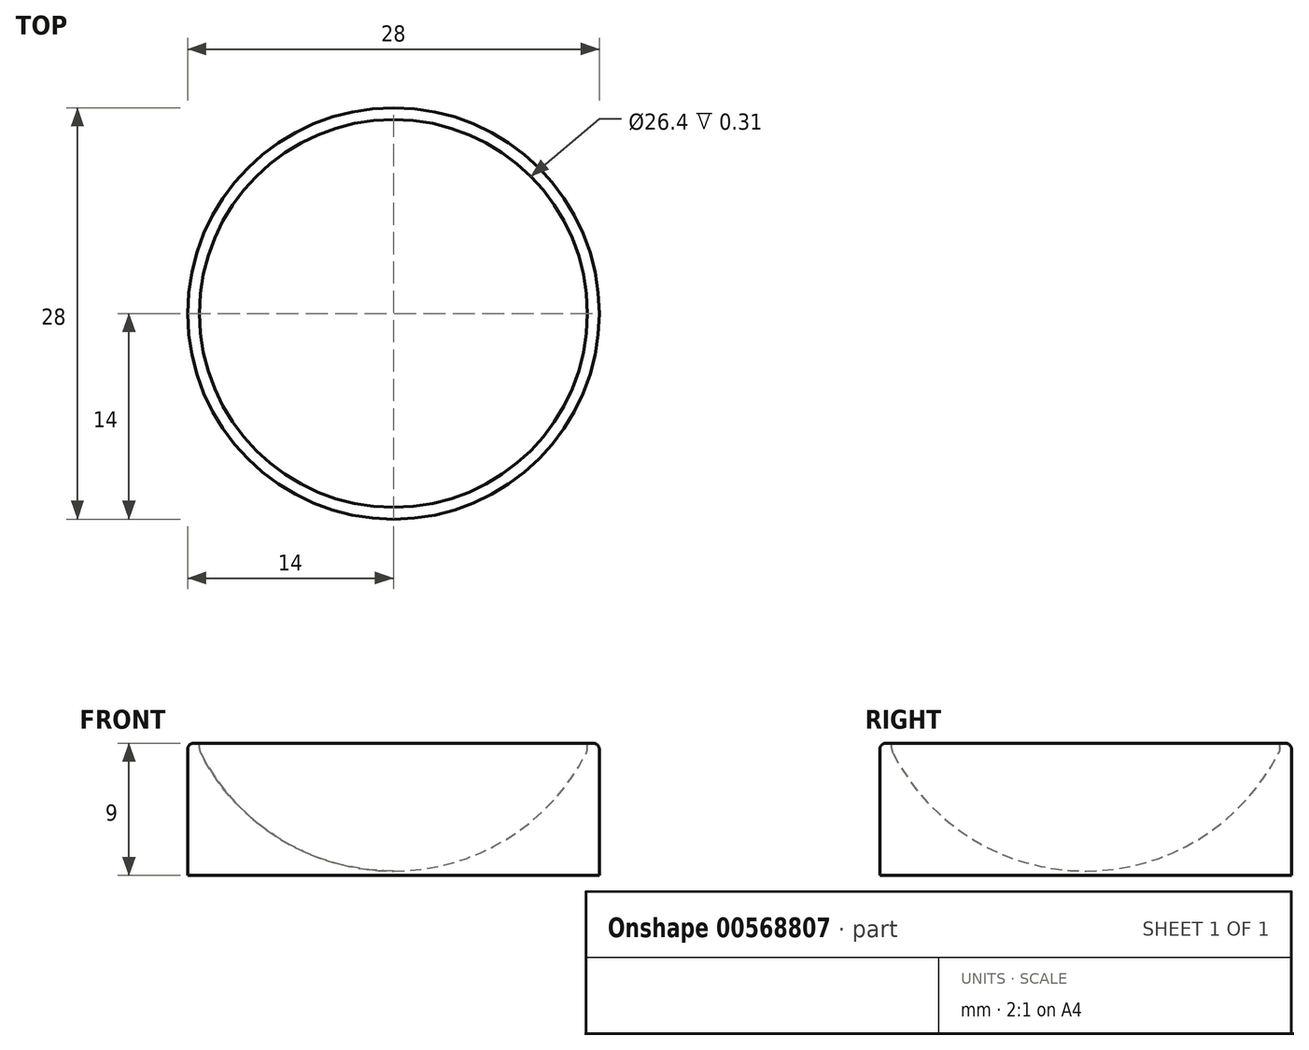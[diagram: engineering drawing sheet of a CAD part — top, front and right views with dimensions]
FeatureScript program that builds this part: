
annotation { "Feature Type Name" : "Feature", "Feature Type Description" : "" }
export const myFeature = defineFeature(function(context is Context, id is Id, definition is map)
    precondition{}
    {
        {
            var Q0;
            Q0=qCreatedBy(makeId("Front.planeOp"),FACE);
            var sketch = newSketch(context, id + "F0", { "sketchPlane" : qUnion([Q0])});
            skLineSegment(sketch, "E0", {"start": v(-14, 0) * mm, "end": v(-14, 9) * mm});
            skLineSegment(sketch, "E1", {"start": v(-14, 9) * mm, "end": v(-13.2, 9) * mm});
            skLineSegment(sketch, "E2", {"start": v(-13.2, 9) * mm, "end": v(-13.2, 8.5) * mm});
            skLineSegment(sketch, "E3", {"start": v(0, 0.3) * mm, "end": v(0, 0) * mm});
            skLineSegment(sketch, "E4", {"start": v(0, 0) * mm, "end": v(-14, 0) * mm});
            skArc(sketch, "E5", {"start": v(-13.2, 8.5) * mm, "mid": v(-7.77, 2.52) * mm, "end": v(0, 0.3) * mm});
            skSolve(sketch);
        }
        {
            var Q0;
            Q0=makeQuery(id+"F0.imprint","IMPRINT",FACE,{"disambiguationData":[TD([[makeQuery(id+"F0.imprint","IMPRINT",EDGE,{"derivedFrom":sQuery(id+"F0.wireOp",EDGE,"E0")}),-1.0]])]});
            var Q1;
            Q1=sQuery(id+"F0.wireOp",EDGE,"E3");
            revolve(context, id + "F1", {"entities" : qUnion([Q0]), "axis" : qUnion([Q1]), "revolveType" : RevolveType.FULL});
        }
        {
            var Q0;
            Q0=makeQuery(id+"F1.opRevolve","SWEPT_EDGE",EDGE,{"disambiguationData":[OSD([sQuery(id+"F0.wireOp",EDGE,"E0"),sQuery(id+"F0.wireOp",EDGE,"E1")])]});
            fillet(context, id + "F2", {"entities" : qUnion([Q0]), "radius" : 0.4 * mm, "tangentPropagation" : true, "allowEdgeOverflow" : false});
        }
        {
            var Q0;
            Q0=makeQuery(id+"F1.opRevolve","SWEPT_EDGE",EDGE,{"disambiguationData":[OSD([sQuery(id+"F0.wireOp",EDGE,"E2"),sQuery(id+"F0.wireOp",EDGE,"E5")])]});
            fillet(context, id + "F3", {"entities" : qUnion([Q0]), "radius" : 0.8 * mm, "tangentPropagation" : true, "allowEdgeOverflow" : false});
        }
    });
